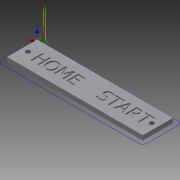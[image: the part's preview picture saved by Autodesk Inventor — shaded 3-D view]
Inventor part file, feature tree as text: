
AUTODESK INVENTOR PART (.ipt)
format: ipt  version: 2015 SP1 (Build 190203100, 203)  size: 356,352 bytes
history: native  units: mm
features: extrude x2, hole x2, sketch x2
ambient origin geometry x8: Origin, YZ Plane, XZ Plane, XY Plane, X Axis, Y Axis, Z Axis, Center Point
bodies: Solid1 (feature_tree)
feature tree (6):
  extrude  "Extrusion1"  Depth=20.0mm
  extrude  "Extrusion2"  Depth=8.0mm
  hole  "Hole1"  [1 undecoded]
  hole  "Hole2"  [1 undecoded]
  sketch  "Sketch1"  dims[d0=90.0mm d1=20.0mm]
  sketch  "Sketch2"  dims[d2=10.0mm d3=45.0mm d4=3.0mm d5=0.0mm d6=1.0mm d7=0.0mm d8=4.0mm d9=10.0mm d10=3.0mm d11=6.0mm d12=4.0mm d13=2.0mm d14=90.0deg d15=8.0mm d16=20.594885mm d17=4.0mm d18=10.0mm d19=3.0mm d20=6.0mm d21=4.0mm d22=2.0mm d23=90.0deg d24=8.0mm d25=20.594885mm]
note: 2 required parameter values undecoded (feature->parameter linkage not recoverable at this tier; creation-order binding heuristic only, values carry confidence <= 0.55)
